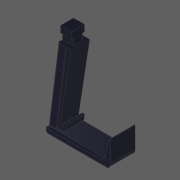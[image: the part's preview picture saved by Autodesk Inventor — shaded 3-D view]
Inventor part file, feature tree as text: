
AUTODESK INVENTOR PART (.ipt)
format: ipt  version: 2020 (Build 240168000, 168)  size: 271,360 bytes
history: native  units: in
note: dims shown in document units (in); Inventor stores cm internally (conversion verified against a paired STEP export)
features: fillet x5, other x3, extrude x3
ambient origin geometry x8: Origin, YZ Plane, XZ Plane, XY Plane, X Axis, Y Axis, Z Axis, Center Point
bodies: Solid1 (feature_tree)
feature tree (11):
  other  "Neck Start Plane"
  other  "Arm Profile"
  extrude  "Main Arm"  Depth=0.0039in
  extrude  "Pincher"  Depth=1.0386in
  extrude  "Neck"  Depth=0.7283in
  fillet  "Spring Hook Fillet"  Radius=0.1181in
  fillet  "Spring Attachment Fillet"  [1 undecoded]
  fillet  "Soft Edges"  Radius=0.195in
  fillet  "Pincher Fillet 1"  Radius=0.0197in
  fillet  "Pincher Fillet 2"  Radius=0.0394in
  other  "Neck Sketch"
note: 1 required parameter value undecoded (feature->parameter linkage not recoverable at this tier; creation-order binding heuristic only, values carry confidence <= 0.55)
